# Revit family: Haworth_CabanaLounge_CollaborativeSofa_TwoArms
name_source: partatom
category: Furniture
revit_build: Autodesk Revit 2018 (Build: 20170223_1515(x64)
units: mm (PartAtom-declared; Revit-internal decimal feet)

## family parameters
Always vertical = Yes
Cut with Voids When Loaded = No
OmniClass Number = 23.40.70.14.64.21
OmniClass Title = Systems Furniture
Room Calculation Point = No
Shared = No
Work Plane-Based = No

## types (6) — shared parameters
Assembly Code = E2020200
Leg Offset = 2 3/4"
Manufacturer = Haworth
Model = Haworth Cabana
Revision Number = 1
Screen Width = 38"
Seat Depth = 30"
Seat Height = 18 1/16"
Seat Width = 72"
Size = Verify Final Dim. w/ Haworth
URL = http://www.haworth.com
URL - Product = https://www.haworth.com
Warranty = http://www.haworth.com

## per-type parameters (varying)
| type | Actual Depth | Actual Height | Actual Width | Alignment Clip Control | Description | High Screen | Low Screen | No Screen | With Screen | With Top |
| S9C2-H - High Screen - With Integrated Table | 32" | 54" | 76" | Yes | Haworth Cabana Collaborative Sofa Two Seats - Two Arms - High Screen - With Integrated Table | Yes | No | No | Yes | Yes |
| S9C2-L - Low Screen - With Integrated Table | 32" | 42" | 76" | Yes | Haworth Cabana Collaborative Sofa Two Seats - Two Arms - Low Screen - With Integrated Table | No | Yes | No | Yes | Yes |
| S9C2-H - High Screen - Without Integrated Table | 32" | 54" | 76" | Yes | Haworth Cabana Collaborative Sofa Two Seats - Two Arms - High Screen - Without Integrated Table | Yes | No | No | Yes | No |
| S9C2-L - Low Screen - Without Integrated Table | 32" | 42" | 76" | Yes | Haworth Cabana Collaborative Sofa Two Seats - Two Arms - Low Screen - Without Integrated Table | No | Yes | No | Yes | No |
| S9C2-0 - No Screen - Without Integrated Table | 30" | 30 3/8" | 72" | No | Haworth Cabana Collaborative Sofa Two Seats - Two Arms - No Screen - Without Integrated Table | No | No | Yes | No | No |
| S9C2-0 - No Screen - With Integrated Table | 30" | 30 3/8" | 72" | No | Haworth Cabana Collaborative Sofa Two Seats - Two Arms - No Screen - With Integrated Table | No | No | Yes | No | Yes |

## geometry (parser evidence)
native form markers: Extrusion x2, Sweep x16
no freeform markers — native parametric forms only
